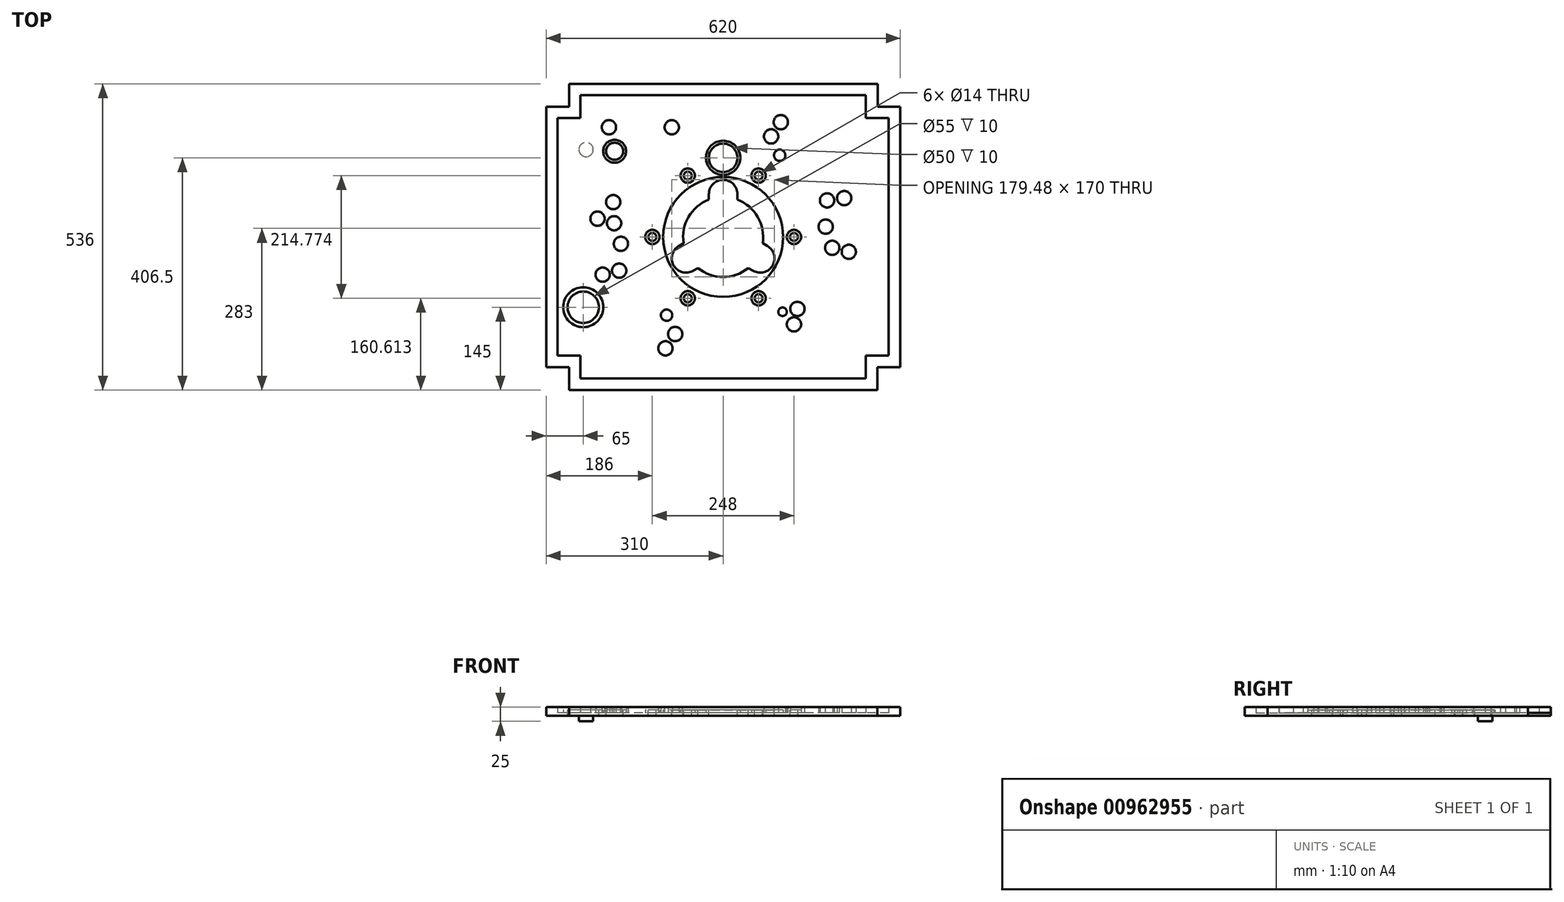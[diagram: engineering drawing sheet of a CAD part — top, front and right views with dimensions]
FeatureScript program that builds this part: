
annotation { "Feature Type Name" : "Feature", "Feature Type Description" : "" }
export const myFeature = defineFeature(function(context is Context, id is Id, definition is map)
    precondition{}
    {
        {
            var Q0;
            Q0=qCreatedBy(makeId("Top.planeOp"),FACE);
            var sketch = newSketch(context, id + "F0", { "sketchPlane" : qUnion([Q0])});
            skLineSegment(sketch, "E0.bottom", {"start": v(-270, -268) * mm, "end": v(270, -268) * mm});
            skLineSegment(sketch, "E0.top", {"start": v(-270, 268) * mm, "end": v(270, 268) * mm});
            skLineSegment(sketch, "E0.left", {"start": v(-310, -228) * mm, "end": v(-310, 228) * mm});
            skLineSegment(sketch, "E0.right", {"start": v(310, -228) * mm, "end": v(310, 228) * mm});
            skPoint(sketch, "E0.middle", {"position": v(0, 0) * mm});
            skLineSegment(sketch, "E1.top", {"start": v(-310, -228) * mm, "end": v(-270, -228) * mm});
            skLineSegment(sketch, "E1.right", {"start": v(-270, -268) * mm, "end": v(-270, -228) * mm});
            skLineSegment(sketch, "E2.top", {"start": v(-310, 228) * mm, "end": v(-270, 228) * mm});
            skLineSegment(sketch, "E2.right", {"start": v(-270, 268) * mm, "end": v(-270, 228) * mm});
            skLineSegment(sketch, "E3.top", {"start": v(310, 228) * mm, "end": v(270, 228) * mm});
            skLineSegment(sketch, "E3.right", {"start": v(270, 268) * mm, "end": v(270, 228) * mm});
            skLineSegment(sketch, "E4.top", {"start": v(310, -228) * mm, "end": v(270, -228) * mm});
            skLineSegment(sketch, "E4.right", {"start": v(270, -268) * mm, "end": v(270, -228) * mm});
            skPoint(sketch, "E5.orphan", {"position": v(-310, 268) * mm});
            skPoint(sketch, "E1.left.start.orphan", {"position": v(-310, -268) * mm});
            skPoint(sketch, "E6.orphan", {"position": v(310, -268) * mm});
            skPoint(sketch, "E3.left.start.orphan", {"position": v(310, 268) * mm});
            skSolve(sketch);
        }
        {
            var Q0;
            Q0 = qSketchRegion(id + "F0", true);
            extrude(context, id + "F1", {"entities" : qUnion([Q0]), "depth" : 5 * mm, "offsetDistance" : 25 * mm});
        }
        {
            var Q0;
            Q0=makeQuery(id+"F1.opExtrude","CAP_FACE",FACE,{"disambiguationData":[OSD([sQuery(id+"F0.wireOp",EDGE,"E0.bottom"),sQuery(id+"F0.wireOp",EDGE,"E0.top"),sQuery(id+"F0.wireOp",EDGE,"E0.left"),sQuery(id+"F0.wireOp",EDGE,"E0.right"),sQuery(id+"F0.wireOp",EDGE,"E1.top"),sQuery(id+"F0.wireOp",EDGE,"E1.right"),sQuery(id+"F0.wireOp",EDGE,"E2.top"),sQuery(id+"F0.wireOp",EDGE,"E2.right"),sQuery(id+"F0.wireOp",EDGE,"E3.top"),sQuery(id+"F0.wireOp",EDGE,"E3.right"),sQuery(id+"F0.wireOp",EDGE,"E4.top"),sQuery(id+"F0.wireOp",EDGE,"E4.right")])],"isStart":false});
            var sketch = newSketch(context, id + "F2", { "sketchPlane" : qUnion([Q0])});
            skLineSegment(sketch, "E7.bottom", {"start": v(-270, -268) * mm, "end": v(270, -268) * mm});
            skLineSegment(sketch, "E7.top", {"start": v(-270, 268) * mm, "end": v(270.79, 268) * mm});
            skLineSegment(sketch, "E7.left", {"start": v(-310, -228) * mm, "end": v(-310, 228) * mm});
            skLineSegment(sketch, "E7.right", {"start": v(310, -228) * mm, "end": v(310, 228) * mm});
            skPoint(sketch, "E7.middle", {"position": v(0, 0) * mm});
            skLineSegment(sketch, "E8.top", {"start": v(-310, -228) * mm, "end": v(-270, -228) * mm});
            skLineSegment(sketch, "E8.right", {"start": v(-270, -268) * mm, "end": v(-270, -228) * mm});
            skLineSegment(sketch, "E9.top", {"start": v(-310, 228) * mm, "end": v(-270, 228) * mm});
            skLineSegment(sketch, "E9.right", {"start": v(-270, 268) * mm, "end": v(-270, 228) * mm});
            skLineSegment(sketch, "E10.top", {"start": v(310, 228) * mm, "end": v(270.79, 228) * mm});
            skLineSegment(sketch, "E10.right", {"start": v(270.79, 268) * mm, "end": v(270.79, 228) * mm});
            skLineSegment(sketch, "E11.top", {"start": v(310, -228) * mm, "end": v(270, -228) * mm});
            skLineSegment(sketch, "E11.right", {"start": v(270, -268) * mm, "end": v(270, -228) * mm});
            skPoint(sketch, "E12.orphan", {"position": v(-310, 268) * mm});
            skPoint(sketch, "E8.left.start.orphan", {"position": v(-310, -268) * mm});
            skPoint(sketch, "E13.orphan", {"position": v(310, -268) * mm});
            skPoint(sketch, "E10.left.start.orphan", {"position": v(310, 268) * mm});
            skLineSegment(sketch, "E14.0", {"start": v(250, 208) * mm, "end": v(250, 248) * mm});
            skLineSegment(sketch, "E14.1", {"start": v(-290, -208) * mm, "end": v(-250, -208) * mm});
            skLineSegment(sketch, "E14.2", {"start": v(-290, 208) * mm, "end": v(-290, -208) * mm});
            skLineSegment(sketch, "E14.3", {"start": v(-250, 208) * mm, "end": v(-290, 208) * mm});
            skLineSegment(sketch, "E14.4", {"start": v(-250, 248) * mm, "end": v(-250, 208) * mm});
            skLineSegment(sketch, "E14.5", {"start": v(-250, -208) * mm, "end": v(-250, -248) * mm});
            skLineSegment(sketch, "E14.6", {"start": v(250, 248) * mm, "end": v(-250, 248) * mm});
            skLineSegment(sketch, "E14.7", {"start": v(-250, -248) * mm, "end": v(250, -248) * mm});
            skLineSegment(sketch, "E14.8", {"start": v(250, -248) * mm, "end": v(250, -208) * mm});
            skLineSegment(sketch, "E14.9", {"start": v(250, -208) * mm, "end": v(290, -208) * mm});
            skLineSegment(sketch, "E14.10", {"start": v(290, -208) * mm, "end": v(290, 208) * mm});
            skLineSegment(sketch, "E14.11", {"start": v(290, 208) * mm, "end": v(250, 208) * mm});
            skSolve(sketch);
        }
        {
            var Q0;
            Q0 = qSketchRegion(id + "F2", true);
            extrude(context, id + "F3", {"entities" : qUnion([Q0]), "operationType" : NewBodyOperationType.ADD, "depth" : 10 * mm, "offsetDistance" : 25 * mm});
        }
        {
            var Q0;
            Q0=makeQuery(id+"F1.opExtrude","CAP_FACE",FACE,{"disambiguationData":[OSD([sQuery(id+"F0.wireOp",EDGE,"E0.bottom"),sQuery(id+"F0.wireOp",EDGE,"E0.top"),sQuery(id+"F0.wireOp",EDGE,"E0.left"),sQuery(id+"F0.wireOp",EDGE,"E0.right"),sQuery(id+"F0.wireOp",EDGE,"E1.top"),sQuery(id+"F0.wireOp",EDGE,"E1.right"),sQuery(id+"F0.wireOp",EDGE,"E2.top"),sQuery(id+"F0.wireOp",EDGE,"E2.right"),sQuery(id+"F0.wireOp",EDGE,"E3.top"),sQuery(id+"F0.wireOp",EDGE,"E3.right"),sQuery(id+"F0.wireOp",EDGE,"E4.top"),sQuery(id+"F0.wireOp",EDGE,"E4.right")])],"isStart":false});
            var sketch = newSketch(context, id + "F4", { "sketchPlane" : qUnion([Q0])});
            skCircle(sketch, "E15", {"center": v(0, 0) * mm, "radius": 105 * mm});
            skCircle(sketch, "E16", {"center": v(0, 138.5) * mm, "radius": 30 * mm});
            skCircle(sketch, "E17", {"center": v(-245, -123) * mm, "radius": 35 * mm});
            skCircle(sketch, "E18", {"center": v(-190, 150) * mm, "radius": 20 * mm});
            skCircle(sketch, "E19", {"center": v(-124, 0) * mm, "radius": 12.5 * mm});
            skCircle(sketch, "E20.1.0", {"center": v(-62, -107.39) * mm, "radius": 12.5 * mm});
            skCircle(sketch, "E20.2.0", {"center": v(62, -107.39) * mm, "radius": 12.5 * mm});
            skCircle(sketch, "E20.3.0", {"center": v(124, 0) * mm, "radius": 12.5 * mm});
            skCircle(sketch, "E20.4.0", {"center": v(62, 107.39) * mm, "radius": 12.5 * mm});
            skCircle(sketch, "E20.5.0", {"center": v(-62, 107.39) * mm, "radius": 12.5 * mm});
            skSolve(sketch);
        }
        {
            var Q0;
            Q0=makeQuery(id+"F4.imprint","IMPRINT",FACE,{"disambiguationData":[TD([[makeQuery(id+"F4.imprint","IMPRINT",EDGE,{"derivedFrom":sQuery(id+"F4.wireOp",EDGE,"E18")}),1.0]])]});
            var Q1;
            Q1=makeQuery(id+"F4.imprint","IMPRINT",FACE,{"disambiguationData":[TD([[makeQuery(id+"F4.imprint","IMPRINT",EDGE,{"derivedFrom":sQuery(id+"F4.wireOp",EDGE,"E16")}),1.0]])]});
            var Q2;
            Q2=makeQuery(id+"F4.imprint","IMPRINT",FACE,{"disambiguationData":[TD([[makeQuery(id+"F4.imprint","IMPRINT",EDGE,{"derivedFrom":sQuery(id+"F4.wireOp",EDGE,"E15")}),1.0]])]});
            var Q3;
            Q3=makeQuery(id+"F4.imprint","IMPRINT",FACE,{"disambiguationData":[TD([[makeQuery(id+"F4.imprint","IMPRINT",EDGE,{"derivedFrom":sQuery(id+"F4.wireOp",EDGE,"E19")}),1.0]])]});
            var Q4;
            Q4=makeQuery(id+"F4.imprint","IMPRINT",FACE,{"disambiguationData":[TD([[makeQuery(id+"F4.imprint","IMPRINT",EDGE,{"derivedFrom":sQuery(id+"F4.wireOp",EDGE,"E17")}),1.0]])]});
            var Q5;
            Q5=makeQuery(id+"F4.imprint","IMPRINT",FACE,{"disambiguationData":[TD([[makeQuery(id+"F4.imprint","IMPRINT",EDGE,{"derivedFrom":sQuery(id+"F4.wireOp",EDGE,"E20.5.0")}),1.0]])]});
            var Q6;
            Q6=makeQuery(id+"F4.imprint","IMPRINT",FACE,{"disambiguationData":[TD([[makeQuery(id+"F4.imprint","IMPRINT",EDGE,{"derivedFrom":sQuery(id+"F4.wireOp",EDGE,"E20.4.0")}),1.0]])]});
            var Q7;
            Q7=makeQuery(id+"F4.imprint","IMPRINT",FACE,{"disambiguationData":[TD([[makeQuery(id+"F4.imprint","IMPRINT",EDGE,{"derivedFrom":sQuery(id+"F4.wireOp",EDGE,"E20.3.0")}),1.0]])]});
            var Q8;
            Q8=makeQuery(id+"F4.imprint","IMPRINT",FACE,{"disambiguationData":[TD([[makeQuery(id+"F4.imprint","IMPRINT",EDGE,{"derivedFrom":sQuery(id+"F4.wireOp",EDGE,"E20.2.0")}),1.0]])]});
            var Q9;
            Q9=makeQuery(id+"F4.imprint","IMPRINT",FACE,{"disambiguationData":[TD([[makeQuery(id+"F4.imprint","IMPRINT",EDGE,{"derivedFrom":sQuery(id+"F4.wireOp",EDGE,"E20.1.0")}),1.0]])]});
            extrude(context, id + "F5", {"entities" : qUnion([Q0, Q1, Q2, Q3, Q4, Q5, Q6, Q7, Q8, Q9]), "operationType" : NewBodyOperationType.ADD, "depth" : 5 * mm, "offsetDistance" : 25 * mm});
        }
        {
            var Q0;
            Q0=makeQuery(id+"F5.opExtrude","CAP_FACE",FACE,{"disambiguationData":[OSD([sQuery(id+"F4.wireOp",EDGE,"E17")])],"isStart":false});
            var sketch = newSketch(context, id + "F6", { "sketchPlane" : qUnion([Q0])});
            skCircle(sketch, "E21", {"center": v(-245, -123) * mm, "radius": 27.5 * mm});
            skCircle(sketch, "E22", {"center": v(-124, 0) * mm, "radius": 7 * mm});
            skCircle(sketch, "E23", {"center": v(0, 138.5) * mm, "radius": 25 * mm});
            skCircle(sketch, "E24", {"center": v(-190, 150) * mm, "radius": 15 * mm});
            skCircle(sketch, "E25.1.0", {"center": v(-62, -107.39) * mm, "radius": 7 * mm});
            skCircle(sketch, "E25.2.0", {"center": v(62, -107.39) * mm, "radius": 7 * mm});
            skCircle(sketch, "E25.3.0", {"center": v(124, 0) * mm, "radius": 7 * mm});
            skCircle(sketch, "E25.4.0", {"center": v(62, 107.39) * mm, "radius": 7 * mm});
            skCircle(sketch, "E25.5.0", {"center": v(-62, 107.39) * mm, "radius": 7 * mm});
            skPoint(sketch, "E25.center", {"position": v(0, 0) * mm});
            skArc(sketch, "E26", {"start": v(25, 75) * mm, "mid": v(0, 100) * mm, "end": v(-25, 75) * mm});
            skLineSegment(sketch, "E27", {"start": v(-25, 75) * mm, "end": v(-25, 65.38) * mm});
            skLineSegment(sketch, "E28", {"start": v(25, 75) * mm, "end": v(25, 65.38) * mm});
            skArc(sketch, "E29.trimOffspring", {"start": v(-25, 65.38) * mm, "mid": v(-60.62, 35) * mm, "end": v(-69.12, -11.04) * mm});
            skLineSegment(sketch, "E30.1.0", {"start": v(-52.45, -59.15) * mm, "end": v(-44.12, -54.34) * mm});
            skArc(sketch, "E30.1.1", {"start": v(-77.45, -15.85) * mm, "mid": v(-86.6, -50) * mm, "end": v(-52.45, -59.15) * mm});
            skLineSegment(sketch, "E30.1.2", {"start": v(-77.45, -15.85) * mm, "end": v(-69.12, -11.04) * mm});
            skLineSegment(sketch, "E30.2.0", {"start": v(77.45, -15.85) * mm, "end": v(69.12, -11.04) * mm});
            skArc(sketch, "E30.2.1", {"start": v(52.45, -59.15) * mm, "mid": v(86.6, -50) * mm, "end": v(77.45, -15.85) * mm});
            skLineSegment(sketch, "E30.2.2", {"start": v(52.45, -59.15) * mm, "end": v(44.12, -54.34) * mm});
            skArc(sketch, "E31.trimOffspring", {"start": v(-44.12, -54.34) * mm, "mid": v(0, -70) * mm, "end": v(44.12, -54.34) * mm});
            skArc(sketch, "E32.trimOffspring", {"start": v(69.12, -11.04) * mm, "mid": v(60.62, 35) * mm, "end": v(25, 65.38) * mm});
            skSolve(sketch);
        }
        {
            var Q0;
            Q0 = qSketchRegion(id + "F6", true);
            extrude(context, id + "F7", {"entities" : qUnion([Q0]), "operationType" : NewBodyOperationType.REMOVE, "endBound" : BoundingType.UP_TO_NEXT, "oppositeDirection" : true, "depth" : 25 * mm, "offsetDistance" : 25 * mm});
        }
        {
            var Q0;
            Q0=makeQuery(id+"F1.opExtrude","CAP_FACE",FACE,{"disambiguationData":[OSD([sQuery(id+"F0.wireOp",EDGE,"E0.bottom"),sQuery(id+"F0.wireOp",EDGE,"E0.top"),sQuery(id+"F0.wireOp",EDGE,"E0.left"),sQuery(id+"F0.wireOp",EDGE,"E0.right"),sQuery(id+"F0.wireOp",EDGE,"E1.top"),sQuery(id+"F0.wireOp",EDGE,"E1.right"),sQuery(id+"F0.wireOp",EDGE,"E2.top"),sQuery(id+"F0.wireOp",EDGE,"E2.right"),sQuery(id+"F0.wireOp",EDGE,"E3.top"),sQuery(id+"F0.wireOp",EDGE,"E3.right"),sQuery(id+"F0.wireOp",EDGE,"E4.top"),sQuery(id+"F0.wireOp",EDGE,"E4.right")])],"isStart":false});
            var sketch = newSketch(context, id + "F8", { "sketchPlane" : qUnion([Q0])});
            skCircle(sketch, "E33", {"center": v(-101, -195) * mm, "radius": 12.5 * mm});
            skCircle(sketch, "E34", {"center": v(-84, -170) * mm, "radius": 12.5 * mm});
            skCircle(sketch, "E35", {"center": v(-179, -12) * mm, "radius": 12.5 * mm});
            skCircle(sketch, "E36", {"center": v(-211, -66) * mm, "radius": 12.5 * mm});
            skCircle(sketch, "E37", {"center": v(-182, -59) * mm, "radius": 12.5 * mm});
            skCircle(sketch, "E38", {"center": v(-220, 32) * mm, "radius": 12.5 * mm});
            skCircle(sketch, "E39", {"center": v(-191, 24) * mm, "radius": 12.5 * mm});
            skCircle(sketch, "E40", {"center": v(-192.5, 61) * mm, "radius": 12.5 * mm});
            skCircle(sketch, "E41", {"center": v(-200, 192) * mm, "radius": 12.5 * mm});
            skCircle(sketch, "E42", {"center": v(-90, 192) * mm, "radius": 12.5 * mm});
            skCircle(sketch, "E43", {"center": v(84, 176) * mm, "radius": 12.5 * mm});
            skCircle(sketch, "E44", {"center": v(101, 201) * mm, "radius": 12.5 * mm});
            skCircle(sketch, "E45", {"center": v(182, 64) * mm, "radius": 12.5 * mm});
            skCircle(sketch, "E46", {"center": v(212, 68) * mm, "radius": 12.5 * mm});
            skCircle(sketch, "E47", {"center": v(179.5, 18) * mm, "radius": 12.5 * mm});
            skCircle(sketch, "E48", {"center": v(191, -19) * mm, "radius": 12.5 * mm});
            skCircle(sketch, "E49", {"center": v(220, -26) * mm, "radius": 12.5 * mm});
            skCircle(sketch, "E50", {"center": v(124, -153) * mm, "radius": 12.5 * mm});
            skCircle(sketch, "E51", {"center": v(130, -126) * mm, "radius": 12.5 * mm});
            skCircle(sketch, "E52", {"center": v(-99, -137) * mm, "radius": 10 * mm});
            skCircle(sketch, "E53", {"center": v(99, 143) * mm, "radius": 10 * mm});
            skCircle(sketch, "E54", {"center": v(104, -131) * mm, "radius": 7.5 * mm});
            skSolve(sketch);
        }
        {
            var Q0;
            Q0 = qSketchRegion(id + "F8", true);
            extrude(context, id + "F9", {"entities" : qUnion([Q0]), "operationType" : NewBodyOperationType.ADD, "depth" : 10 * mm, "offsetDistance" : 25 * mm});
        }
        {
            var Q0;
            Q0=makeQuery(id+"F1.opExtrude","CAP_FACE",FACE,{"disambiguationData":[OSD([sQuery(id+"F0.wireOp",EDGE,"E0.bottom"),sQuery(id+"F0.wireOp",EDGE,"E0.top"),sQuery(id+"F0.wireOp",EDGE,"E0.left"),sQuery(id+"F0.wireOp",EDGE,"E0.right"),sQuery(id+"F0.wireOp",EDGE,"E1.top"),sQuery(id+"F0.wireOp",EDGE,"E1.right"),sQuery(id+"F0.wireOp",EDGE,"E2.top"),sQuery(id+"F0.wireOp",EDGE,"E2.right"),sQuery(id+"F0.wireOp",EDGE,"E3.top"),sQuery(id+"F0.wireOp",EDGE,"E3.right"),sQuery(id+"F0.wireOp",EDGE,"E4.top"),sQuery(id+"F0.wireOp",EDGE,"E4.right")])],"isStart":true});
            var sketch = newSketch(context, id + "F10", { "sketchPlane" : qUnion([Q0])});
            skCircle(sketch, "E55", {"center": v(-240, -153) * mm, "radius": 12.5 * mm});
            skSolve(sketch);
        }
        {
            var Q0;
            Q0 = qSketchRegion(id + "F10", true);
            extrude(context, id + "F11", {"entities" : qUnion([Q0]), "operationType" : NewBodyOperationType.ADD, "depth" : 10 * mm, "offsetDistance" : 25 * mm});
        }
    });
